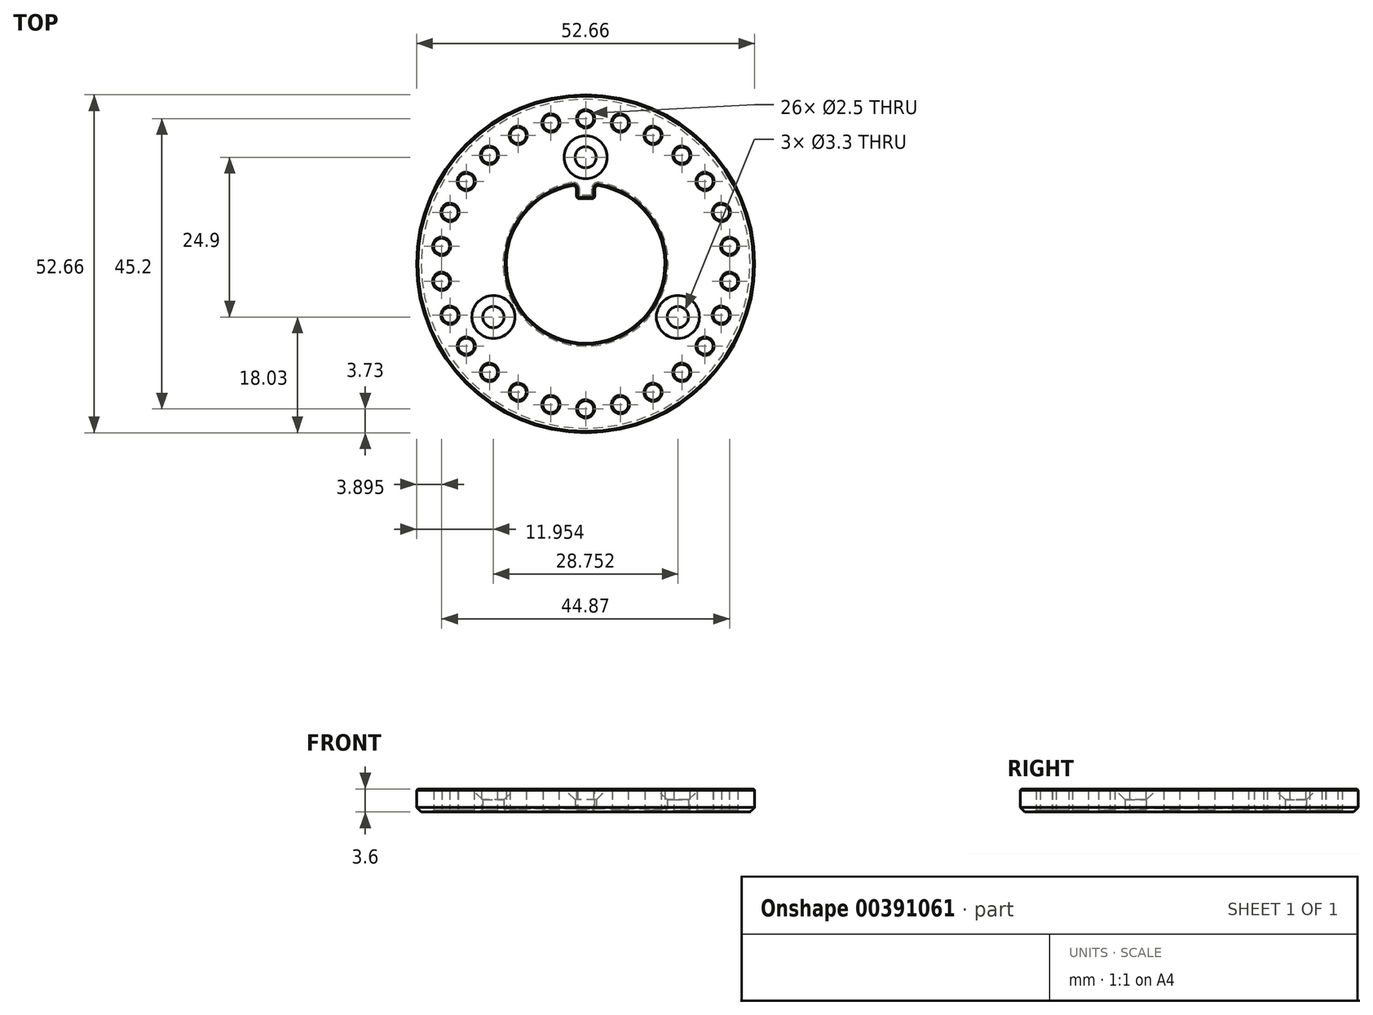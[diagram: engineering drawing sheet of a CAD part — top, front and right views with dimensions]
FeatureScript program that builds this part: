
annotation { "Feature Type Name" : "Feature", "Feature Type Description" : "" }
export const myFeature = defineFeature(function(context is Context, id is Id, definition is map)
    precondition{}
    {
        {
            var Q0;
            Q0=qCreatedBy(makeId("Top.planeOp"),FACE);
            var sketch = newSketch(context, id + "F0", { "sketchPlane" : qUnion([Q0])});
            skCircle(sketch, "E0", {"center": v(0, 0) * mm, "radius": 26.33 * mm});
            skArc(sketch, "E1", {"start": v(-1.45, 12.26) * mm, "mid": v(0, -12.35) * mm, "end": v(1.45, 12.26) * mm});
            skLineSegment(sketch, "E2", {"start": v(0, 0) * mm, "end": v(0, 22.6) * mm, "construction": true});
            skCircle(sketch, "E3", {"center": v(0, 22.6) * mm, "radius": 1.25 * mm});
            skLineSegment(sketch, "E4", {"start": v(0, 0) * mm, "end": v(0, 16.6) * mm, "construction": true});
            skCircle(sketch, "E5", {"center": v(0, 16.6) * mm, "radius": 1.65 * mm});
            skLineSegment(sketch, "E6", {"start": v(-1.45, 12.26) * mm, "end": v(-1.45, 10.15) * mm});
            skLineSegment(sketch, "E7", {"start": v(1.45, 12.26) * mm, "end": v(1.45, 10.15) * mm});
            skLineSegment(sketch, "E8", {"start": v(-1.45, 10.15) * mm, "end": v(1.45, 10.15) * mm});
            skSolve(sketch);
        }
        {
            var Q0;
            Q0=makeQuery(id+"F0.imprint","IMPRINT",FACE,{"disambiguationData":[TD([[makeQuery(id+"F0.imprint","IMPRINT",EDGE,{"derivedFrom":sQuery(id+"F0.wireOp",EDGE,"E0")}),1.0]])]});
            extrude(context, id + "F1", {"entities" : qUnion([Q0]), "depth" : 3.6 * mm});
        }
        {
            var Q0;
            Q0=makeQuery(id+"F1.opExtrude","CAP_EDGE",EDGE,{"disambiguationData":[OSD([sQuery(id+"F0.wireOp",EDGE,"E3")])],"isStart":false});
            chamfer(context, id + "F2", {"entities" : qUnion([Q0]), "width" : .15 * mm, "tangentPropagation" : true});
        }
        {
            var Q0;
            Q0=makeQuery(id+"F1.opExtrude","CAP_EDGE",EDGE,{"disambiguationData":[OSD([sQuery(id+"F0.wireOp",EDGE,"E3")])],"isStart":true});
            chamfer(context, id + "F3", {"entities" : qUnion([Q0]), "width" : .3 * mm, "tangentPropagation" : true});
        }
        {
            var Q0;
            Q0=makeQuery(id+"F1.opExtrude","SWEPT_FACE",FACE,{"disambiguationData":[OSD([sQuery(id+"F0.wireOp",EDGE,"E3")])]});
            var Q1;
            Q1=makeQuery(id+"F3.opChamfer","BLEND_FACE",FACE,{"disambiguationData":[OSD([sQuery(id+"F0.wireOp",EDGE,"E3")])]});
            var Q2;
            Q2=makeQuery(id+"F2.opChamfer","BLEND_FACE",FACE,{"disambiguationData":[OSD([sQuery(id+"F0.wireOp",EDGE,"E3")])]});
            var Q3;
            Q3=makeQuery(id+"F1.opExtrude","CAP_EDGE",EDGE,{"disambiguationData":[OSD([sQuery(id+"F0.wireOp",EDGE,"E0")])],"isStart":false});
            circularPattern(context, id + "F4", {"patternType" : PatternType.FACE, "operationType" : NewBodyOperationType.REMOVE, "faces" : qUnion([Q0, Q1, Q2]), "axis" : qUnion([Q3]), "angle" : 360 * degree, "instanceCount" : 26, "equalSpace" : true});
        }
        {
            var Q0;
            Q0=makeQuery(id+"F1.opExtrude","CAP_EDGE",EDGE,{"disambiguationData":[OSD([sQuery(id+"F0.wireOp",EDGE,"E5")])],"isStart":false});
            chamfer(context, id + "F5", {"entities" : qUnion([Q0]), "width" : 1.7 * mm, "tangentPropagation" : true});
        }
        {
            var Q0;
            Q0=makeQuery(id+"F5.opChamfer","BLEND_FACE",FACE,{"disambiguationData":[OSD([sQuery(id+"F0.wireOp",EDGE,"E5")])]});
            var Q1;
            Q1=makeQuery(id+"F1.opExtrude","SWEPT_FACE",FACE,{"disambiguationData":[OSD([sQuery(id+"F0.wireOp",EDGE,"E5")])]});
            var Q2;
            Q2=makeQuery(id+"F1.opExtrude","CAP_EDGE",EDGE,{"disambiguationData":[OSD([sQuery(id+"F0.wireOp",EDGE,"E0")])],"isStart":false});
            circularPattern(context, id + "F6", {"patternType" : PatternType.FACE, "operationType" : NewBodyOperationType.REMOVE, "faces" : qUnion([Q0, Q1]), "axis" : qUnion([Q2]), "angle" : 360 * degree, "instanceCount" : 3, "equalSpace" : true});
        }
        {
            var Q0;
            Q0=makeQuery(id+"F1.opExtrude","SWEPT_EDGE",EDGE,{"disambiguationData":[OSD([sQuery(id+"F0.wireOp",EDGE,"E7"),sQuery(id+"F0.wireOp",EDGE,"E8")])]});
            var Q1;
            Q1=makeQuery(id+"F1.opExtrude","SWEPT_EDGE",EDGE,{"disambiguationData":[OSD([sQuery(id+"F0.wireOp",EDGE,"E6"),sQuery(id+"F0.wireOp",EDGE,"E8")])]});
            var Q2;
            Q2=makeQuery(id+"F1.opExtrude","SWEPT_EDGE",EDGE,{"disambiguationData":[OSD([sQuery(id+"F0.wireOp",EDGE,"E1"),sQuery(id+"F0.wireOp",EDGE,"E7")])]});
            var Q3;
            Q3=makeQuery(id+"F1.opExtrude","SWEPT_EDGE",EDGE,{"disambiguationData":[OSD([sQuery(id+"F0.wireOp",EDGE,"E1"),sQuery(id+"F0.wireOp",EDGE,"E6")])]});
            fillet(context, id + "F7", {"entities" : qUnion([Q0, Q1, Q2, Q3]), "radius" : 0.5 * mm, "tangentPropagation" : true, "allowEdgeOverflow" : false});
        }
        {
            var Q0;
            Q0=makeQuery(id+"F1.opExtrude","CAP_EDGE",EDGE,{"disambiguationData":[OSD([sQuery(id+"F0.wireOp",EDGE,"E1")])],"isStart":true});
            chamfer(context, id + "F8", {"entities" : qUnion([Q0]), "width" : .5 * mm, "tangentPropagation" : true});
        }
        {
            var Q0;
            Q0=makeQuery(id+"F1.opExtrude","CAP_EDGE",EDGE,{"disambiguationData":[OSD([sQuery(id+"F0.wireOp",EDGE,"E0")])],"isStart":false});
            var Q1;
            Q1=makeQuery(id+"F1.opExtrude","CAP_EDGE",EDGE,{"disambiguationData":[OSD([sQuery(id+"F0.wireOp",EDGE,"E1")])],"isStart":false});
            chamfer(context, id + "F9", {"entities" : qUnion([Q0, Q1]), "width" : .2 * mm, "tangentPropagation" : true});
        }
        {
            var Q0;
            Q0=makeQuery(id+"F1.opExtrude","CAP_EDGE",EDGE,{"disambiguationData":[OSD([sQuery(id+"F0.wireOp",EDGE,"E0")])],"isStart":true});
            chamfer(context, id + "F10", {"entities" : qUnion([Q0]), "width" : .7 * mm, "tangentPropagation" : true});
        }
    });
